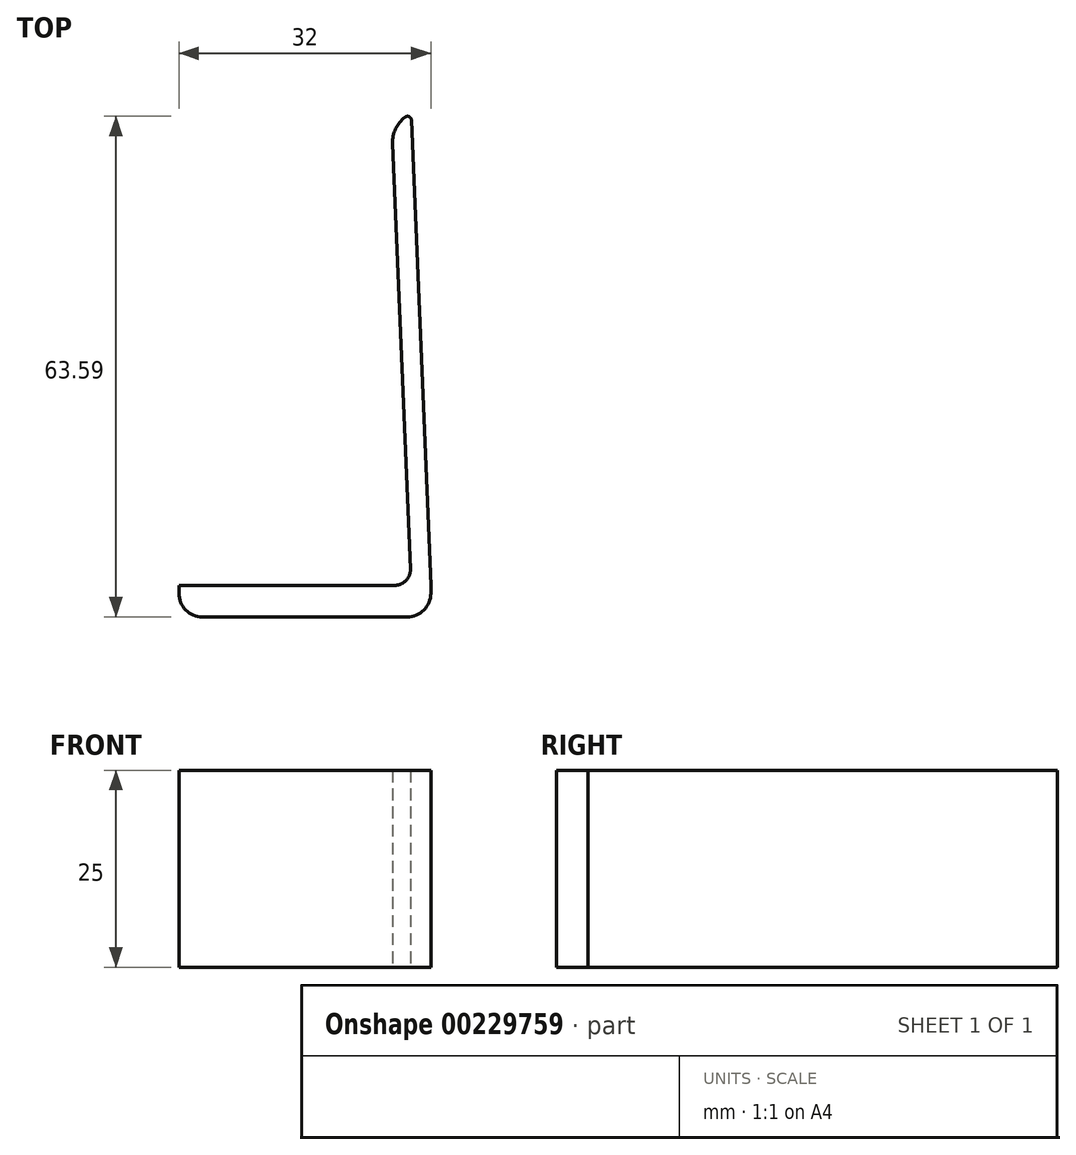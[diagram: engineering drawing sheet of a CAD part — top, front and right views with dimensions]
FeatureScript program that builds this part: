
annotation { "Feature Type Name" : "Feature", "Feature Type Description" : "" }
export const myFeature = defineFeature(function(context is Context, id is Id, definition is map)
    precondition{}
    {
        {
            var Q0;
            Q0=qCreatedBy(makeId("Top.planeOp"),FACE);
            var sketch = newSketch(context, id + "F0", { "sketchPlane" : qUnion([Q0])});
            skLineSegment(sketch, "E0.bottom", {"start": v(16, -2) * mm, "end": v(-16, -2) * mm});
            skLineSegment(sketch, "E0.top", {"start": v(16, 2) * mm, "end": v(-16, 2) * mm});
            skLineSegment(sketch, "E0.left", {"start": v(16, -2) * mm, "end": v(16, 2) * mm});
            skLineSegment(sketch, "E0.right", {"start": v(-16, -2) * mm, "end": v(-16, 2) * mm});
            skPoint(sketch, "E0.middle", {"position": v(0, 0) * mm});
            skLineSegment(sketch, "E1.bottom", {"start": v(-16, 2) * mm, "end": v(-13.5, 2) * mm});
            skLineSegment(sketch, "E1.top", {"start": v(-13.5, 61.95) * mm, "end": v(-11, 61.95) * mm});
            skLineSegment(sketch, "E1.left", {"start": v(-16, 2) * mm, "end": v(-13.5, 61.95) * mm});
            skLineSegment(sketch, "E1.right", {"start": v(-13.5, 2) * mm, "end": v(-11, 61.95) * mm});
            skLineSegment(sketch, "E2.MirrorCS", {"start": v(13.5, 2) * mm, "end": v(11, 61.95) * mm});
            skLineSegment(sketch, "E3.MirrorCS", {"start": v(16, 2) * mm, "end": v(13.5, 61.95) * mm});
            skLineSegment(sketch, "E4.MirrorCS", {"start": v(13.5, 61.95) * mm, "end": v(11, 61.95) * mm});
            skSolve(sketch);
        }
        {
            var Q0;
            Q0=makeQuery(id+"F0.imprint","IMPRINT",FACE,{"disambiguationData":[TD([[makeQuery(id+"F0.imprint","IMPRINT",EDGE,{"derivedFrom":sQuery(id+"F0.wireOp",EDGE,"E1.bottom")}),1.0]])]});
            var Q1;
            {var subQ2=sQuery(id+"F0.wireOp",EDGE,"E2.MirrorCS");Q1=makeQuery(id+"F0.imprint","IMPRINT",FACE,{"disambiguationData":[TD([[makeQuery(id+"F0.imprint","IMPRINT",EDGE,{"derivedFrom":subQ2}),-1.0]])]});}
            var Q2;
            Q2=makeQuery(id+"F0.imprint","IMPRINT",FACE,{"disambiguationData":[TD([[makeQuery(id+"F0.imprint","IMPRINT",EDGE,{"derivedFrom":sQuery(id+"F0.wireOp",EDGE,"E0.bottom")}),-1.0]])]});
            extrude(context, id + "F1", {"entities" : qUnion([Q0, Q1, Q2]), "depth" : 25 * mm});
        }
        {
            var Q0;
            Q0=makeQuery(id+"F1.opExtrude","SWEPT_EDGE",EDGE,{"disambiguationData":[OSD([sQuery(id+"F0.wireOp",EDGE,"E2.MirrorCS"),sQuery(id+"F0.wireOp",EDGE,"E4.MirrorCS")])]});
            var Q1;
            Q1=makeQuery(id+"F1.opExtrude","SWEPT_EDGE",EDGE,{"disambiguationData":[OSD([sQuery(id+"F0.wireOp",EDGE,"E1.top"),sQuery(id+"F0.wireOp",EDGE,"E1.right")])]});
            fillet(context, id + "F2", {"entities" : qUnion([Q0, Q1]), "radius" : 4 * mm, "tangentPropagation" : true, "allowEdgeOverflow" : false});
        }
        {
            var Q0;
            Q0=makeQuery(id+"F2.opFillet","BLEND_EDGE",EDGE,{"blendedFrom":[makeQuery(id+"F1.opExtrude","SWEPT_EDGE",EDGE,{"disambiguationData":[OSD([sQuery(id+"F0.wireOp",EDGE,"E1.top"),sQuery(id+"F0.wireOp",EDGE,"E1.right")])]}),makeQuery(id+"F1.opExtrude","SWEPT_FACE",FACE,{"disambiguationData":[OSD([sQuery(id+"F0.wireOp",EDGE,"E0.right"),sQuery(id+"F0.wireOp",EDGE,"E1.left")])]})],"blendedInto":[makeQuery(id+"F1.opExtrude","SWEPT_FACE",FACE,{"disambiguationData":[OSD([sQuery(id+"F0.wireOp",EDGE,"E0.right"),sQuery(id+"F0.wireOp",EDGE,"E1.left")])]})]});
            var Q1;
            Q1=makeQuery(id+"F2.opFillet","BLEND_EDGE",EDGE,{"blendedFrom":[makeQuery(id+"F1.opExtrude","SWEPT_EDGE",EDGE,{"disambiguationData":[OSD([sQuery(id+"F0.wireOp",EDGE,"E2.MirrorCS"),sQuery(id+"F0.wireOp",EDGE,"E4.MirrorCS")])]}),makeQuery(id+"F1.opExtrude","SWEPT_FACE",FACE,{"disambiguationData":[OSD([sQuery(id+"F0.wireOp",EDGE,"E0.left"),sQuery(id+"F0.wireOp",EDGE,"E3.MirrorCS")])]})],"blendedInto":[makeQuery(id+"F1.opExtrude","SWEPT_FACE",FACE,{"disambiguationData":[OSD([sQuery(id+"F0.wireOp",EDGE,"E0.left"),sQuery(id+"F0.wireOp",EDGE,"E3.MirrorCS")])]})]});
            fillet(context, id + "F3", {"entities" : qUnion([Q0, Q1]), "radius" : .5 * mm, "tangentPropagation" : true, "allowEdgeOverflow" : false});
        }
        {
            var Q0;
            Q0=makeQuery(id+"F1.opExtrude","SWEPT_EDGE",EDGE,{"disambiguationData":[OSD([sQuery(id+"F0.wireOp",EDGE,"E0.bottom"),sQuery(id+"F0.wireOp",EDGE,"E0.left")])]});
            var Q1;
            Q1=makeQuery(id+"F1.opExtrude","SWEPT_EDGE",EDGE,{"disambiguationData":[OSD([sQuery(id+"F0.wireOp",EDGE,"E0.bottom"),sQuery(id+"F0.wireOp",EDGE,"E0.right")])]});
            fillet(context, id + "F4", {"entities" : qUnion([Q0, Q1]), "radius" : 3 * mm, "tangentPropagation" : true, "allowEdgeOverflow" : false});
        }
        {
            var Q0;
            Q0=makeQuery(id+"F1.opExtrude","SWEPT_EDGE",EDGE,{"disambiguationData":[OSD([sQuery(id+"F0.wireOp",EDGE,"E0.top"),sQuery(id+"F0.wireOp",EDGE,"E1.bottom"),sQuery(id+"F0.wireOp",EDGE,"E1.right")])]});
            var Q1;
            Q1=makeQuery(id+"F1.opExtrude","SWEPT_EDGE",EDGE,{"disambiguationData":[OSD([sQuery(id+"F0.wireOp",EDGE,"E0.top"),sQuery(id+"F0.wireOp",EDGE,"E2.MirrorCS")])]});
            fillet(context, id + "F5", {"entities" : qUnion([Q0, Q1]), "radius" : 2 * mm, "tangentPropagation" : true, "allowEdgeOverflow" : false});
        }
    });
